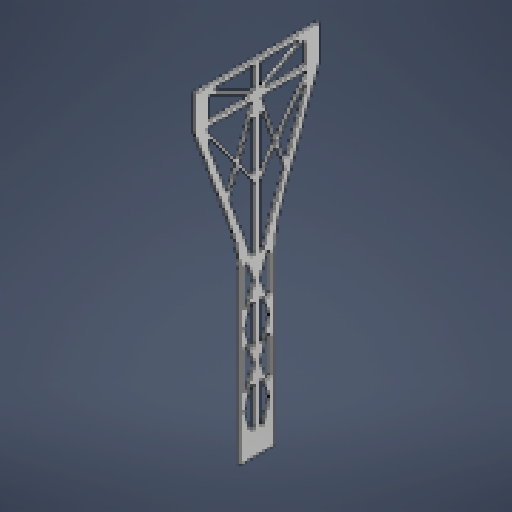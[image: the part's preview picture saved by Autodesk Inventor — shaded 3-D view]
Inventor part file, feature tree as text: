
AUTODESK INVENTOR PART (.ipt)
format: ipt  version: 2024.3 (Build 283343000, 343)  size: 369,152 bytes
history: native  units: mm (DEFAULTED — no unit token found)
features: sketch x2, other x2, sheet_metal_op x1, mirror x1, chamfer x1, projected_geometry x1
ambient origin geometry x8: Origin, YZ Plane, XZ Plane, XY Plane, X Axis, Y Axis, Z Axis, Center Point
bodies: Body1 (feature_tree)
feature tree (8):
  sheet_metal_op  "Face1"
  mirror  "Mirror1"
  chamfer  "Corner Round1"
  sketch  "Sketch2"  dims[d6=177.8mm]
  other  "Plate1"
  sketch  "Sketch3"  dims[d7=596.9mm d8=152.4mm d9=12.217305mm d10=50.8mm d11=25.4mm d12=127.0mm d13=3.175mm d14=19.05mm d15=6.35mm d16=3.175mm d17=38.1mm d18=6.35mm d19=9.525mm d20=6.35mm d21=1.5875mm d23=3.175mm d24=6.35mm d25=6.35mm d26=3.175mm d27=96.515487mm d28=20.0mm d30=102.865487mm d31=10.0mm d33=25.4mm d35=3.175mm d36=0.0mm d37=3.175mm]
  projected_geometry  "Projected Loop1"
  other  "Cut1"
